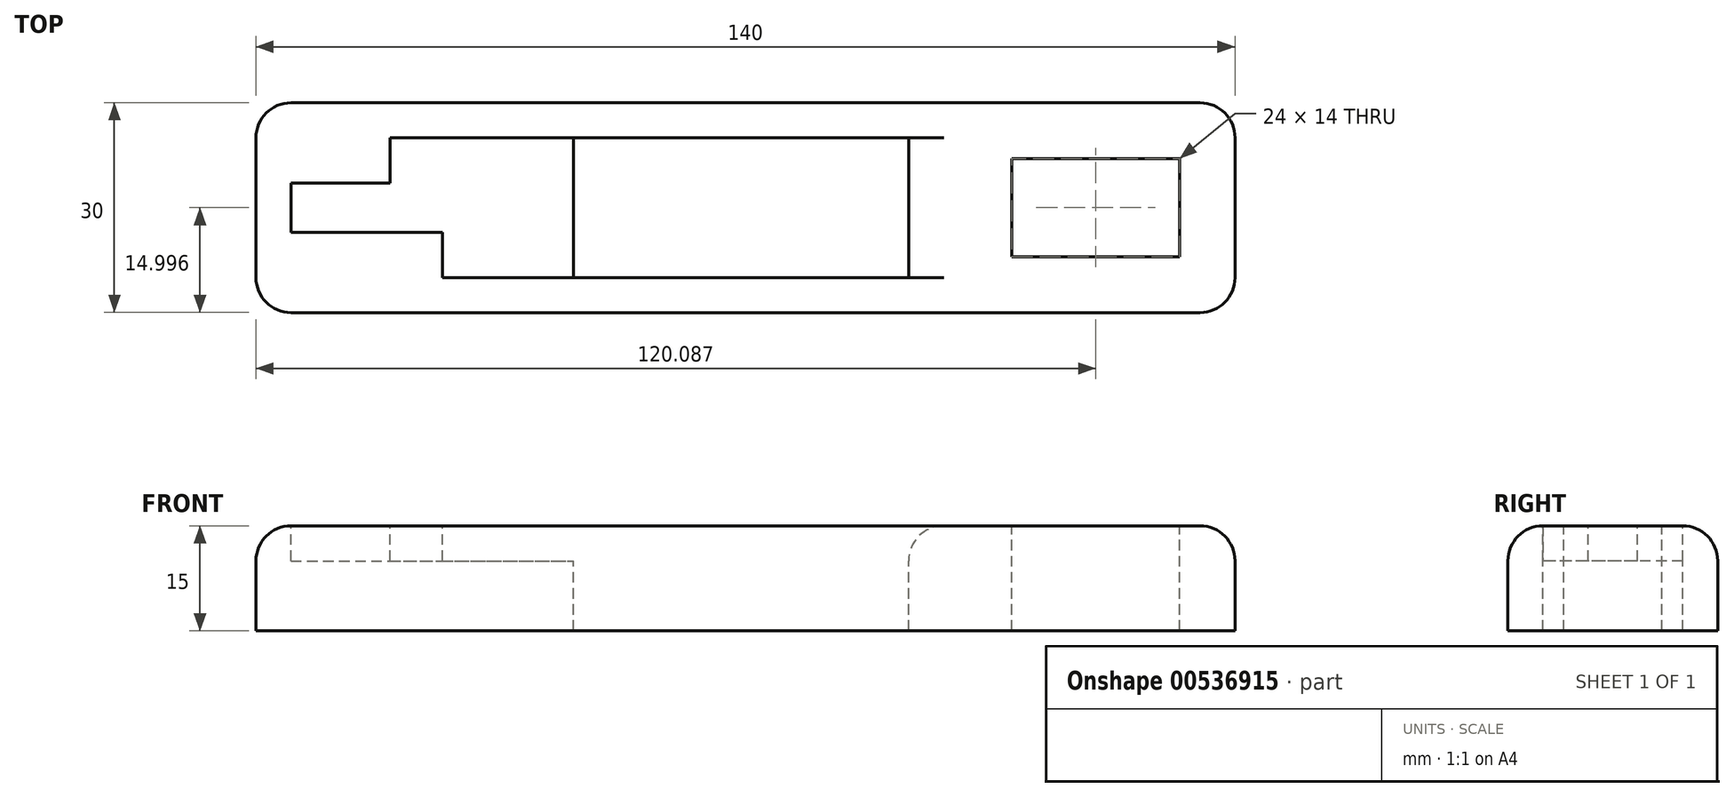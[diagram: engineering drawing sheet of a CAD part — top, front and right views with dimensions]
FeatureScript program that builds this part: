
annotation { "Feature Type Name" : "Feature", "Feature Type Description" : "" }
export const myFeature = defineFeature(function(context is Context, id is Id, definition is map)
    precondition{}
    {
        {
            var Q0;
            Q0=qCreatedBy(makeId("Top.planeOp"),FACE);
            var sketch = newSketch(context, id + "F0", { "sketchPlane" : qUnion([Q0])});
            skLineSegment(sketch, "E0.bottom", {"start": v(-58.35, 16.34) * mm, "end": v(81.65, 16.34) * mm});
            skLineSegment(sketch, "E0.top", {"start": v(-58.35, -13.66) * mm, "end": v(81.65, -13.66) * mm});
            skLineSegment(sketch, "E0.left", {"start": v(-58.35, 16.34) * mm, "end": v(-58.35, -13.66) * mm});
            skLineSegment(sketch, "E0.right", {"start": v(81.65, 16.34) * mm, "end": v(81.65, -13.66) * mm});
            skSolve(sketch);
        }
        {
            var Q0;
            Q0=makeQuery(id+"F0.imprint","IMPRINT",FACE,{"disambiguationData":[TD([[makeQuery(id+"F0.imprint","IMPRINT",EDGE,{"derivedFrom":sQuery(id+"F0.wireOp",EDGE,"E0.bottom")}),-1.0]])]});
            extrude(context, id + "F1", {"entities" : qUnion([Q0]), "depth" : 15 * mm, "offsetDistance" : 25 * mm});
        }
        {
            var Q0;
            Q0=makeQuery(id+"F1.opExtrude","SWEPT_EDGE",EDGE,{"disambiguationData":[OSD([sQuery(id+"F0.wireOp",EDGE,"E0.top"),sQuery(id+"F0.wireOp",EDGE,"E0.right")])]});
            var Q1;
            Q1=makeQuery(id+"F1.opExtrude","SWEPT_EDGE",EDGE,{"disambiguationData":[OSD([sQuery(id+"F0.wireOp",EDGE,"E0.bottom"),sQuery(id+"F0.wireOp",EDGE,"E0.right")])]});
            var Q2;
            Q2=makeQuery(id+"F1.opExtrude","CAP_EDGE",EDGE,{"disambiguationData":[OSD([sQuery(id+"F0.wireOp",EDGE,"E0.right")])],"isStart":false});
            var Q3;
            Q3=makeQuery(id+"F1.opExtrude","CAP_EDGE",EDGE,{"disambiguationData":[OSD([sQuery(id+"F0.wireOp",EDGE,"E0.top")])],"isStart":false});
            var Q4;
            Q4=makeQuery(id+"F1.opExtrude","CAP_EDGE",EDGE,{"disambiguationData":[OSD([sQuery(id+"F0.wireOp",EDGE,"E0.bottom")])],"isStart":false});
            fillet(context, id + "F2", {"entities" : qUnion([Q0, Q1, Q2, Q3, Q4]), "radius" : 5 * mm, "tangentPropagation" : true, "allowEdgeOverflow" : false});
        }
        {
            var Q0;
            Q0=makeQuery(id+"F1.opExtrude","CAP_FACE",FACE,{"disambiguationData":[OSD([sQuery(id+"F0.wireOp",EDGE,"E0.bottom"),sQuery(id+"F0.wireOp",EDGE,"E0.top"),sQuery(id+"F0.wireOp",EDGE,"E0.left"),sQuery(id+"F0.wireOp",EDGE,"E0.right")])],"isStart":false});
            var sketch = newSketch(context, id + "F3", { "sketchPlane" : qUnion([Q0])});
            skLineSegment(sketch, "E1.bottom", {"start": v(-12.95, 11.34) * mm, "end": v(34.98, 11.34) * mm});
            skLineSegment(sketch, "E1.top", {"start": v(-12.95, -8.66) * mm, "end": v(34.98, -8.66) * mm});
            skLineSegment(sketch, "E1.left", {"start": v(-12.95, 11.34) * mm, "end": v(-12.95, -8.66) * mm});
            skLineSegment(sketch, "E1.right", {"start": v(34.98, 11.34) * mm, "end": v(34.98, -8.66) * mm});
            skSolve(sketch);
        }
        {
            var Q0;
            Q0=makeQuery(id+"F3.imprint","IMPRINT",FACE,{"disambiguationData":[TD([[makeQuery(id+"F3.imprint","IMPRINT",EDGE,{"derivedFrom":sQuery(id+"F3.wireOp",EDGE,"E1.bottom")}),1.0]])]});
            extrude(context, id + "F4", {"entities" : qUnion([Q0]), "operationType" : NewBodyOperationType.REMOVE, "oppositeDirection" : true, "depth" : 25 * mm, "offsetDistance" : 25 * mm});
        }
        {
            var Q0;
            Q0=makeQuery(id+"F4.boolean.opBoolean","COPY",EDGE,{"derivedFrom":makeQuery(id+"F4.opExtrude","CAP_EDGE",EDGE,{"disambiguationData":[OSD([sQuery(id+"F3.wireOp",EDGE,"E1.left")])],"isStart":true})});
            var Q1;
            Q1=makeQuery(id+"F4.boolean.opBoolean","COPY",EDGE,{"derivedFrom":makeQuery(id+"F4.opExtrude","CAP_EDGE",EDGE,{"disambiguationData":[OSD([sQuery(id+"F3.wireOp",EDGE,"E1.right")])],"isStart":true})});
            fillet(context, id + "F5", {"entities" : qUnion([Q0, Q1]), "radius" : 5 * mm, "tangentPropagation" : true, "allowEdgeOverflow" : false});
        }
        {
            var Q0;
            Q0=makeQuery(id+"F1.opExtrude","CAP_EDGE",EDGE,{"disambiguationData":[OSD([sQuery(id+"F0.wireOp",EDGE,"E0.left")])],"isStart":false});
            fillet(context, id + "F6", {"entities" : qUnion([Q0]), "radius" : 5 * mm, "tangentPropagation" : true, "allowEdgeOverflow" : false});
        }
        {
            var Q0;
            {var subQ0=sQuery(id+"F0.wireOp",EDGE,"E0.top");var subQ1=sQuery(id+"F0.wireOp",EDGE,"E0.bottom");var subQ2=sQuery(id+"F0.wireOp",EDGE,"E0.left");Q0=makeQuery(id+"F4.boolean.opBoolean","SPLIT",FACE,{"disambiguationData":[TD([makeQuery(id+"F1.opExtrude","SWEPT_FACE",FACE,{"disambiguationData":[OSD([subQ2])]})])],"derivedFrom":makeQuery(id+"F1.opExtrude","CAP_FACE",FACE,{"disambiguationData":[OSD([subQ1,subQ0,subQ2,sQuery(id+"F0.wireOp",EDGE,"E0.right")])],"isStart":false})});}
            var sketch = newSketch(context, id + "F7", { "sketchPlane" : qUnion([Q0])});
            skLineSegment(sketch, "E2.top", {"start": v(-53.35, -8.66) * mm, "end": v(73.74, -8.66) * mm});
            skLineSegment(sketch, "E2.left", {"start": v(-53.35, 1.34) * mm, "end": v(-53.35, -8.66) * mm});
            skLineSegment(sketch, "E3.top", {"start": v(-53.35, 4.88) * mm, "end": v(-17.95, 4.88) * mm});
            skLineSegment(sketch, "E3.left", {"start": v(-53.35, 1.34) * mm, "end": v(-53.35, 4.88) * mm});
            skLineSegment(sketch, "E3.right", {"start": v(-17.95, 1.34) * mm, "end": v(-17.95, 4.88) * mm});
            skLineSegment(sketch, "E4.MirrorCS", {"start": v(-53.35, -2.2) * mm, "end": v(-17.95, -2.2) * mm});
            skLineSegment(sketch, "E5.bottom", {"start": v(39.86, 11.38) * mm, "end": v(58.32, 11.38) * mm});
            skLineSegment(sketch, "E5.top", {"start": v(39.86, -8.66) * mm, "end": v(58.32, -8.66) * mm});
            skLineSegment(sketch, "E5.left", {"start": v(39.86, 11.38) * mm, "end": v(39.86, -8.66) * mm});
            skLineSegment(sketch, "E6.top", {"start": v(73.74, 8.34) * mm, "end": v(49.74, 8.34) * mm});
            skLineSegment(sketch, "E6.left", {"start": v(73.74, 1.34) * mm, "end": v(73.74, 8.34) * mm});
            skLineSegment(sketch, "E6.right", {"start": v(49.74, 1.34) * mm, "end": v(49.74, 8.34) * mm});
            skLineSegment(sketch, "E7.MirrorCS", {"start": v(49.74, 1.34) * mm, "end": v(49.74, -5.66) * mm});
            skLineSegment(sketch, "E8.MirrorCS", {"start": v(73.74, -5.66) * mm, "end": v(49.74, -5.66) * mm});
            skLineSegment(sketch, "E9.MirrorCS", {"start": v(73.74, 1.34) * mm, "end": v(73.74, -5.66) * mm});
            skLineSegment(sketch, "E10.bottom", {"start": v(-39.17, 11.34) * mm, "end": v(-31.65, 11.34) * mm});
            skLineSegment(sketch, "E10.top", {"start": v(-39.17, 4.88) * mm, "end": v(-31.65, 4.88) * mm});
            skLineSegment(sketch, "E10.left", {"start": v(-39.17, 11.34) * mm, "end": v(-39.17, 4.88) * mm});
            skLineSegment(sketch, "E10.right", {"start": v(-31.65, 11.34) * mm, "end": v(-31.65, 4.88) * mm});
            skLineSegment(sketch, "E11.bottom", {"start": v(-39.28, -2.2) * mm, "end": v(-31.65, -2.2) * mm});
            skLineSegment(sketch, "E11.top", {"start": v(-39.28, -8.66) * mm, "end": v(-31.65, -8.66) * mm});
            skLineSegment(sketch, "E11.left", {"start": v(-39.28, -2.2) * mm, "end": v(-39.28, -8.66) * mm});
            skLineSegment(sketch, "E11.right", {"start": v(-31.65, -2.2) * mm, "end": v(-31.65, -8.66) * mm});
            skSolve(sketch);
        }
        {
            var Q0;
            Q0=makeQuery(id+"F7.imprint","IMPRINT",FACE,{"disambiguationData":[TD([[makeQuery(id+"F7.imprint","IMPRINT",EDGE,{"derivedFrom":sQuery(id+"F7.wireOp",EDGE,"E6.top")}),1.0]])]});
            extrude(context, id + "F8", {"entities" : qUnion([Q0]), "operationType" : NewBodyOperationType.REMOVE, "oppositeDirection" : true, "depth" : 25 * mm, "offsetDistance" : 25 * mm});
        }
        {
            var Q0;
            Q0=makeQuery(id+"F7.imprint","IMPRINT",FACE,{"disambiguationData":[TD([[makeQuery(id+"F7.imprint","IMPRINT",EDGE,{"derivedFrom":sQuery(id+"F7.wireOp",EDGE,"E3.top")}),-1.0]])]});
            var Q1;
            Q1=makeQuery(id+"F7.imprint","IMPRINT",FACE,{"disambiguationData":[TD([[makeQuery(id+"F7.imprint","IMPRINT",EDGE,{"derivedFrom":sQuery(id+"F7.wireOp",EDGE,"E10.bottom")}),1.0]])]});
            var Q2;
            Q2=makeQuery(id+"F7.imprint","IMPRINT",FACE,{"disambiguationData":[TD([[makeQuery(id+"F7.imprint","IMPRINT",EDGE,{"derivedFrom":sQuery(id+"F7.wireOp",EDGE,"E11.bottom")}),-1.0]])]});
            extrude(context, id + "F9", {"entities" : qUnion([Q0, Q1, Q2]), "operationType" : NewBodyOperationType.REMOVE, "oppositeDirection" : true, "depth" : 5 * mm, "offsetDistance" : 25 * mm});
        }
    });
